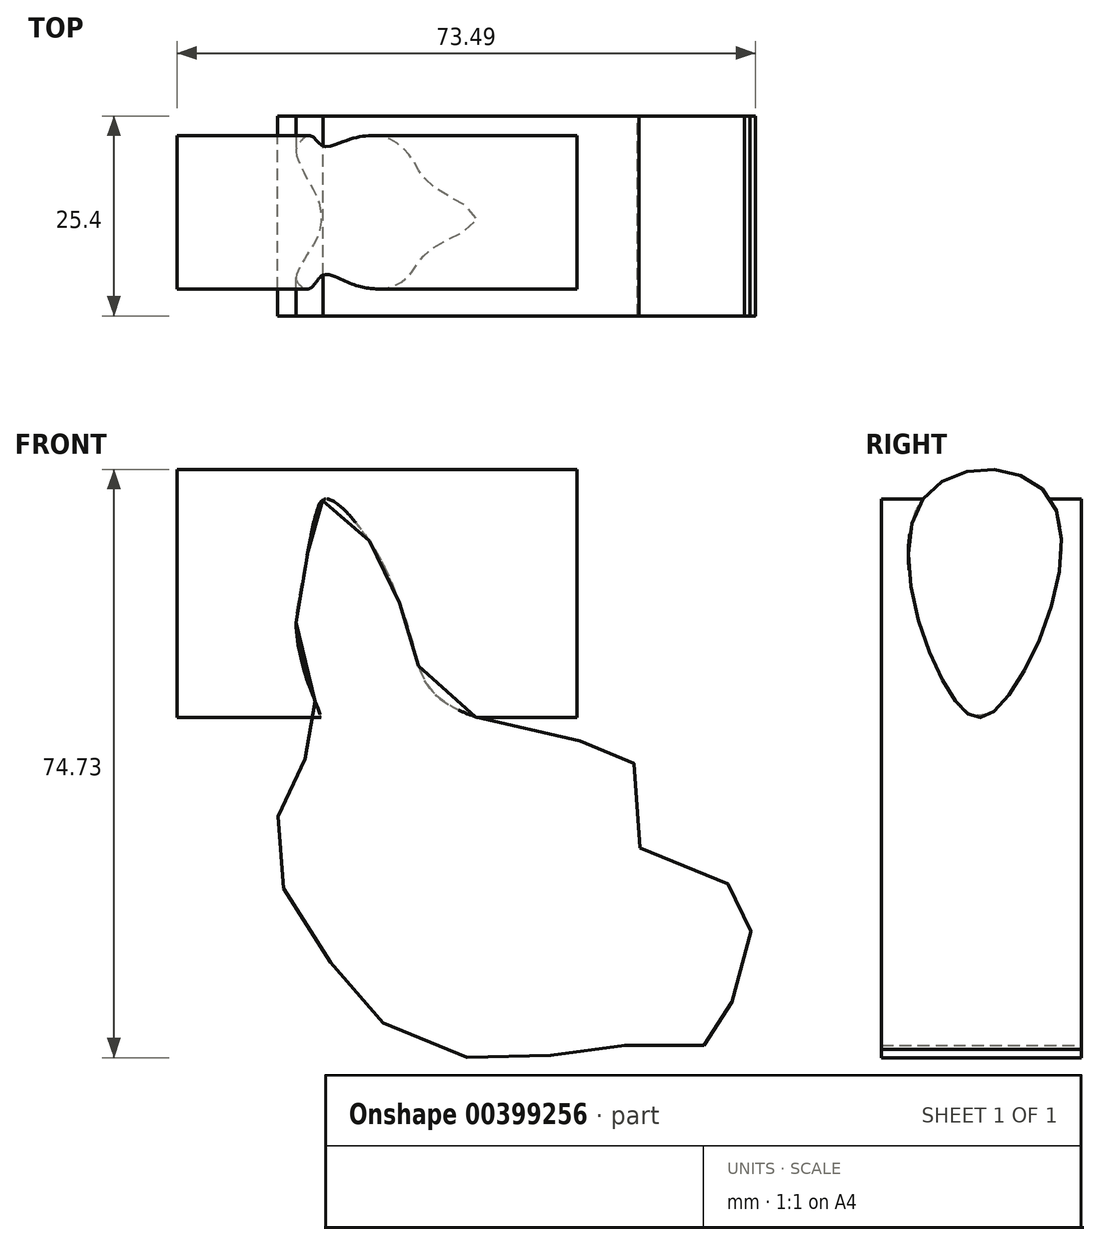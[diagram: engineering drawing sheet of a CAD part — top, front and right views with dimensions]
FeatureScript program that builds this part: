
annotation { "Feature Type Name" : "Feature", "Feature Type Description" : "" }
export const myFeature = defineFeature(function(context is Context, id is Id, definition is map)
    precondition{}
    {
        {
            var Q0;
            Q0=qCreatedBy(makeId("Front.planeOp"),FACE);
            var sketch = newSketch(context, id + "F0", { "sketchPlane" : qUnion([Q0])});
            skFitSpline(sketch, "E0", {"points": [v(8, 4.38) * mm, v(10.86, 3.2) * mm, v(21.98, -2.53) * mm, v(21.3, -4.21) * mm, v(22.49, -7.24) * mm, v(21.14, -13.98) * mm, v(18.78, -16.17) * mm, v(18.44, -18.7) * mm, v(15.08, -21.06) * mm, v(10.02, -20.89) * mm, v(0.76, -21.06) * mm, v(-2.61, -21.9) * mm, v(-10.02, -22.24) * mm, v(-16.09, -21.9) * mm, v(-24.34, -18.03) * mm, v(-28.89, -13.81) * mm, v(-33.1, -7.41) * mm, v(-37.14, -1.01) * mm, v(-37.98, 5.22) * mm, v(-37.82, 9.1) * mm, v(-35.96, 13.64) * mm, v(-34.1, 16.17) * mm, v(-32.26, 19.03) * mm, v(-33.94, 24.76) * mm, v(-35.63, 31.83) * mm, v(-35.46, 35.03) * mm, v(-34.28, 41.44) * mm, v(-33.6, 44.8) * mm, v(-32.76, 47.84) * mm, v(-31.92, 48.68) * mm, v(-29.56, 47.33) * mm, v(-25.35, 41.77) * mm, v(-23.67, 38.4) * mm, v(-21.64, 33.01) * mm, v(-20.63, 29.48) * mm, v(-19.12, 25.26) * mm, v(-13.9, 21.4) * mm, v(-1.1, 18.19) * mm, v(2.61, 17.52) * mm, v(6.49, 15.83) * mm, v(7.83, 13.3) * mm, v(8, 4.38) * mm]});
            skSolve(sketch);
        }
        {
            var Q0;
            Q0 = qSketchRegion(id + "F0", true);
            extrude(context, id + "F1", {"entities" : qUnion([Q0]), "depth" : 25.4 * mm});
        }
        {
            var Q0;
            Q0=qCreatedBy(makeId("Right.planeOp"),FACE);
            var sketch = newSketch(context, id + "F2", { "sketchPlane" : qUnion([Q0])});
            skFitSpline(sketch, "E1", {"points": [v(-20.13, 48.68) * mm, v(-15.92, 22.9) * mm, v(-10.7, 22.06) * mm, v(-3.79, 48.5) * mm, v(-20.13, 48.68) * mm]});
            skSolve(sketch);
        }
        {
            var Q0;
            Q0 = qSketchRegion(id + "F2", true);
            extrude(context, id + "F3", {"entities" : qUnion([Q0]), "operationType" : NewBodyOperationType.ADD, "depth" : -50.8 * mm});
        }
    });
